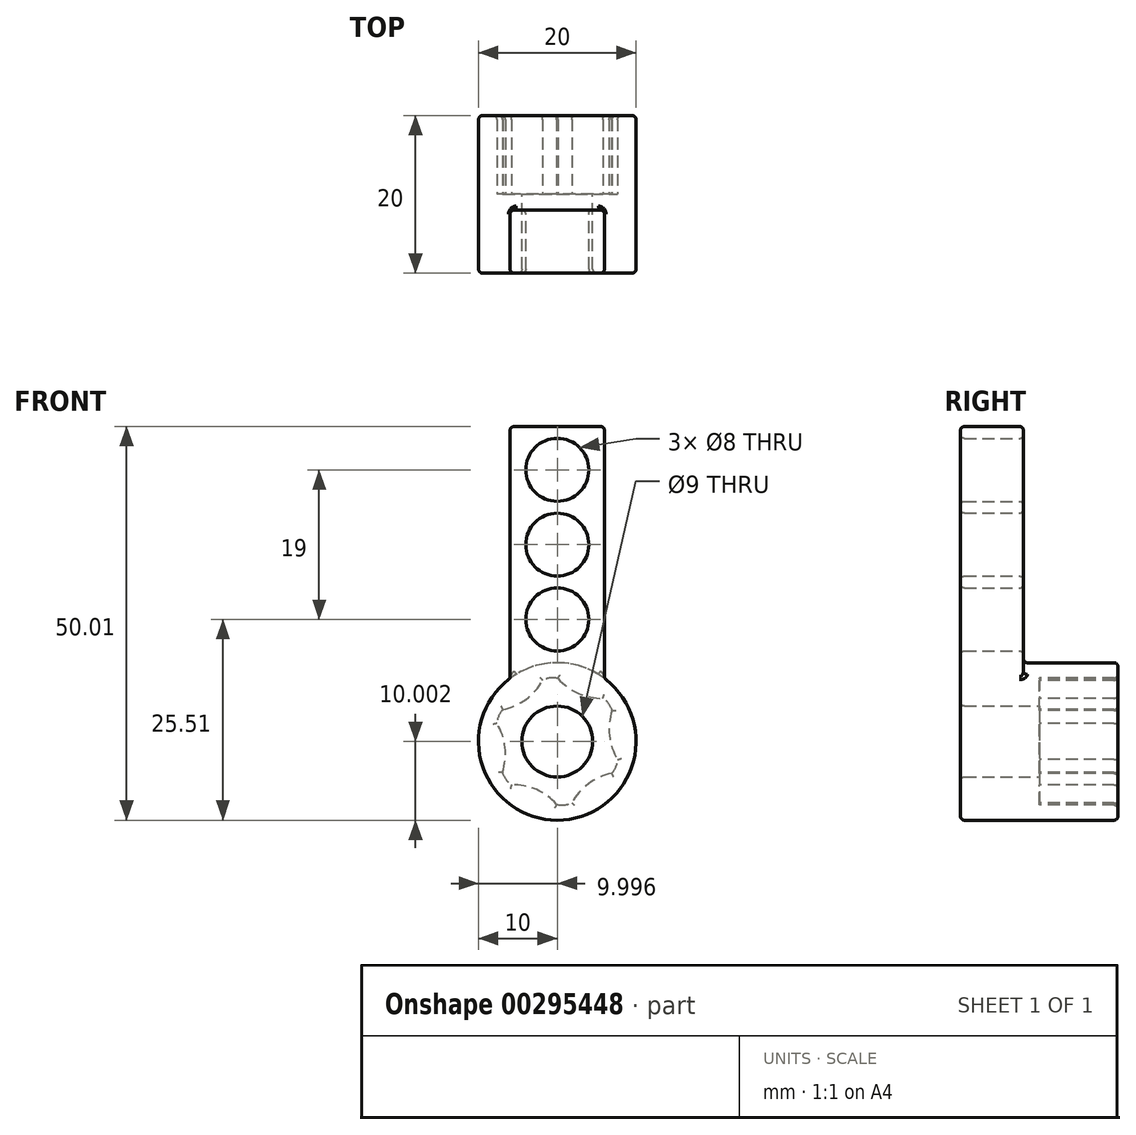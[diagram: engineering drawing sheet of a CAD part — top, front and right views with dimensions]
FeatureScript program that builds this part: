
annotation { "Feature Type Name" : "Feature", "Feature Type Description" : "" }
export const myFeature = defineFeature(function(context is Context, id is Id, definition is map)
    precondition{}
    {
        {
            var Q0;
            Q0=qCreatedBy(makeId("Front.planeOp"),FACE);
            var sketch = newSketch(context, id + "F0", { "sketchPlane" : qUnion([Q0])});
            skArc(sketch, "E0", {"start": v(0.06, 8) * mm, "mid": v(-0.91, 8.06) * mm, "end": v(-1.85, 7.78) * mm});
            skArc(sketch, "E1", {"start": v(6.96, 3.93) * mm, "mid": v(6.53, 4.81) * mm, "end": v(5.81, 5.48) * mm});
            skArc(sketch, "E2", {"start": v(0.06, 8) * mm, "mid": v(2.66, 6.1) * mm, "end": v(5.81, 5.48) * mm});
            skArc(sketch, "E3", {"start": v(-6.9, 4.05) * mm, "mid": v(-3.97, 5.36) * mm, "end": v(-1.85, 7.78) * mm});
            skArc(sketch, "E4", {"start": v(-6.97, -3.95) * mm, "mid": v(-6.63, -0.76) * mm, "end": v(-7.67, 2.28) * mm});
            skArc(sketch, "E5", {"start": v(-0.07, -8) * mm, "mid": v(-2.67, -6.12) * mm, "end": v(-5.82, -5.5) * mm});
            skArc(sketch, "E6", {"start": v(6.9, -4.07) * mm, "mid": v(3.96, -5.38) * mm, "end": v(1.84, -7.8) * mm});
            skArc(sketch, "E7", {"start": v(6.96, 3.93) * mm, "mid": v(6.63, 0.74) * mm, "end": v(7.66, -2.3) * mm});
            skCircle(sketch, "E8", {"center": v(0, 0) * mm, "radius": 10 * mm});
            skPoint(sketch, "E9.0.midPoint", {"position": v(2.1, 4.8) * mm});
            skCircle(sketch, "E10.cCircle", {"center": v(0, 0) * mm, "radius": 4.6 * mm, "construction": true});
            skLineSegment(sketch, "E10.0", {"start": v(0.6, -5.29) * mm, "end": v(-4.28, -3.16) * mm});
            skLineSegment(sketch, "E10.1", {"start": v(-4.28, -3.16) * mm, "end": v(-4.87, 2.12) * mm});
            skLineSegment(sketch, "E10.2", {"start": v(-4.87, 2.12) * mm, "end": v(-0.6, 5.27) * mm});
            skLineSegment(sketch, "E10.3", {"start": v(-0.6, 5.27) * mm, "end": v(4.27, 3.15) * mm});
            skLineSegment(sketch, "E10.4", {"start": v(4.27, 3.15) * mm, "end": v(4.87, -2.13) * mm});
            skLineSegment(sketch, "E10.5", {"start": v(4.87, -2.13) * mm, "end": v(0.6, -5.29) * mm});
            skPoint(sketch, "E10.0.midPoint", {"position": v(-1.84, -4.22) * mm});
            skArc(sketch, "E11.trimOffspring", {"start": v(6.9, -4.07) * mm, "mid": v(7.44, -3.25) * mm, "end": v(7.66, -2.3) * mm});
            skArc(sketch, "E12.trimOffspring", {"start": v(-0.07, -8) * mm, "mid": v(0.9, -8.07) * mm, "end": v(1.84, -7.8) * mm});
            skArc(sketch, "E13.trimOffspring", {"start": v(-6.97, -3.95) * mm, "mid": v(-6.53, -4.83) * mm, "end": v(-5.82, -5.5) * mm});
            skArc(sketch, "E14.trimOffspring", {"start": v(-6.9, 4.05) * mm, "mid": v(-7.44, 3.24) * mm, "end": v(-7.67, 2.28) * mm});
            skPoint(sketch, "E15.orphan", {"position": v(4.87, 3.6) * mm});
            skPoint(sketch, "E9.0.start.orphan", {"position": v(-0.68, 6.02) * mm});
            skSolve(sketch);
        }
        {
            var Q0;
            Q0=makeQuery(id+"F0.imprint","IMPRINT",FACE,{"disambiguationData":[TD([[makeQuery(id+"F0.imprint","IMPRINT",EDGE,{"derivedFrom":sQuery(id+"F0.wireOp",EDGE,"E0")}),-1.0]])]});
            var Q1;
            Q1=makeQuery(id+"F0.imprint","IMPRINT",FACE,{"disambiguationData":[TD([[makeQuery(id+"F0.imprint","IMPRINT",EDGE,{"derivedFrom":sQuery(id+"F0.wireOp",EDGE,"E10.0")}),-1.0]])]});
            var Q2;
            Q2=makeQuery(id+"F0.imprint","IMPRINT",FACE,{"disambiguationData":[TD([[makeQuery(id+"F0.imprint","IMPRINT",EDGE,{"derivedFrom":sQuery(id+"F0.wireOp",EDGE,"E0")}),1.0]])]});
            extrude(context, id + "F1", {"entities" : qUnion([Q0, Q1, Q2]), "offsetDistance" : 25 * mm, "depth" : 2 * mm});
        }
        {
            var Q0;
            Q0=makeQuery(id+"F0.imprint","IMPRINT",FACE,{"disambiguationData":[TD([[makeQuery(id+"F0.imprint","IMPRINT",EDGE,{"derivedFrom":sQuery(id+"F0.wireOp",EDGE,"E0")}),-1.0]])]});
            extrude(context, id + "F2", {"entities" : qUnion([Q0]), "operationType" : NewBodyOperationType.ADD, "oppositeDirection" : true, "offsetDistance" : 25 * mm, "depth" : 10 * mm});
        }
        {
            var Q0;
            Q0=makeQuery(id+"F1.opExtrude","CAP_FACE",FACE,{"disambiguationData":[OSD([sQuery(id+"F0.wireOp",EDGE,"E8")])],"isStart":false});
            var sketch = newSketch(context, id + "F3", { "sketchPlane" : qUnion([Q0])});
            skLineSegment(sketch, "E16", {"start": v(0, 0) * mm, "end": v(0, -10) * mm});
            skLineSegment(sketch, "E17", {"start": v(0, -10) * mm, "end": v(0, 10) * mm});
            skLineSegment(sketch, "E18.bottom", {"start": v(0, 0) * mm, "end": v(6, 0) * mm});
            skLineSegment(sketch, "E18.top", {"start": v(0, 40) * mm, "end": v(6, 40) * mm});
            skLineSegment(sketch, "E18.left", {"start": v(0, 0) * mm, "end": v(0, 40) * mm});
            skLineSegment(sketch, "E18.right", {"start": v(6, 0) * mm, "end": v(6, 40) * mm});
            skLineSegment(sketch, "E19.bottom", {"start": v(0, 0) * mm, "end": v(-6, 0) * mm});
            skLineSegment(sketch, "E19.top", {"start": v(0, 40) * mm, "end": v(-6, 40) * mm});
            skLineSegment(sketch, "E19.right", {"start": v(-6, 0) * mm, "end": v(-6, 40) * mm});
            skLineSegment(sketch, "E20.bottom", {"start": v(-6, 0) * mm, "end": v(6, 0) * mm});
            skCircle(sketch, "E21", {"center": v(0, 34.5) * mm, "radius": 4 * mm});
            skCircle(sketch, "E22", {"center": v(0, 25) * mm, "radius": 4 * mm});
            skCircle(sketch, "E23", {"center": v(0, 15.5) * mm, "radius": 4 * mm});
            skSolve(sketch);
        }
        {
            var Q0;
            {var subQ1=sQuery(id+"F3.wireOp",EDGE,"E20.top");Q0=makeQuery(id+"F3.imprint","IMPRINT",FACE,{"disambiguationData":[TD([[makeQuery(id+"F3.imprint","IMPRINT",EDGE,{"derivedFrom":subQ1}),1.0]])]});}
            var Q1;
            {var subQ0=sQuery(id+"F3.wireOp",EDGE,"E19.top");Q1=makeQuery(id+"F3.imprint","IMPRINT",FACE,{"disambiguationData":[TD([[makeQuery(id+"F3.imprint","IMPRINT",EDGE,{"derivedFrom":subQ0}),1.0]])]});}
            var Q2;
            {var subQ0=sQuery(id+"F3.wireOp",EDGE,"E18.top");Q2=makeQuery(id+"F3.imprint","IMPRINT",FACE,{"disambiguationData":[TD([[makeQuery(id+"F3.imprint","IMPRINT",EDGE,{"derivedFrom":subQ0}),-1.0]])]});}
            var Q3;
            {var subQ1=sQuery(id+"F3.wireOp",EDGE,"E18.right");var subQ3=makeQuery(id+"F1.opExtrude","CAP_EDGE",EDGE,{"disambiguationData":[OSD([sQuery(id+"F0.wireOp",EDGE,"E8")])],"isStart":false});var subQ4=makeQuery(id+"F3.imprint","INTERSECT",VERTEX,{"derivedFrom":[subQ3,subQ1]});Q3=makeQuery(id+"F3.imprint","IMPRINT",FACE,{"disambiguationData":[TD([[makeQuery(id+"F3.imprint","IMPRINT",EDGE,{"disambiguationData":[TD([[subQ4,1.0]])],"derivedFrom":subQ3}),1.0]])]});}
            var Q4;
            {var subQ1=sQuery(id+"F3.wireOp",EDGE,"E19.right");var subQ3=makeQuery(id+"F1.opExtrude","CAP_EDGE",EDGE,{"disambiguationData":[OSD([sQuery(id+"F0.wireOp",EDGE,"E8")])],"isStart":false});var subQ4=makeQuery(id+"F3.imprint","INTERSECT",VERTEX,{"derivedFrom":[subQ3,subQ1]});Q4=makeQuery(id+"F3.imprint","IMPRINT",FACE,{"disambiguationData":[TD([[makeQuery(id+"F3.imprint","IMPRINT",EDGE,{"disambiguationData":[TD([[subQ4,-1.0]])],"derivedFrom":subQ3}),1.0]])]});}
            var Q5;
            {var subQ1=sQuery(id+"F3.wireOp",EDGE,"E18.left");var subQ3=makeQuery(id+"F1.opExtrude","CAP_EDGE",EDGE,{"disambiguationData":[OSD([sQuery(id+"F0.wireOp",EDGE,"E8")])],"isStart":false});var subQ4=makeQuery(id+"F3.imprint","INTERSECT",VERTEX,{"derivedFrom":[subQ3,subQ1]});Q5=makeQuery(id+"F3.imprint","IMPRINT",FACE,{"disambiguationData":[TD([[makeQuery(id+"F3.imprint","IMPRINT",EDGE,{"disambiguationData":[TD([[subQ4,-1.0]])],"derivedFrom":subQ3}),1.0]])]});}
            var Q6;
            {var subQ3=makeQuery(id+"F1.opExtrude","CAP_EDGE",EDGE,{"disambiguationData":[OSD([sQuery(id+"F0.wireOp",EDGE,"E8")])],"isStart":false});var subQ5=sQuery(id+"F3.wireOp",EDGE,"E18.left");var subQ7=makeQuery(id+"F3.imprint","INTERSECT",VERTEX,{"derivedFrom":[subQ3,subQ5]});Q6=makeQuery(id+"F3.imprint","IMPRINT",FACE,{"disambiguationData":[TD([[makeQuery(id+"F3.imprint","IMPRINT",EDGE,{"disambiguationData":[TD([[subQ7,1.0]])],"derivedFrom":subQ3}),1.0]])]});}
            var Q7;
            {var subQ0=sQuery(id+"F3.wireOp",EDGE,"E17");var subQ1=makeQuery(id+"F1.opExtrude","CAP_EDGE",EDGE,{"disambiguationData":[OSD([sQuery(id+"F0.wireOp",EDGE,"E8")])],"isStart":false});var subQ2=makeQuery(id+"F3.imprint","INTERSECT",VERTEX,{"derivedFrom":[subQ1,subQ0]});Q7=makeQuery(id+"F3.imprint","IMPRINT",FACE,{"disambiguationData":[TD([[makeQuery(id+"F3.imprint","IMPRINT",EDGE,{"disambiguationData":[TD([[subQ2,1.0]])],"derivedFrom":subQ1}),1.0]])]});}
            var Q8;
            {var subQ0=sQuery(id+"F3.wireOp",EDGE,"E17");var subQ1=makeQuery(id+"F1.opExtrude","CAP_EDGE",EDGE,{"disambiguationData":[OSD([sQuery(id+"F0.wireOp",EDGE,"E8")])],"isStart":false});var subQ2=makeQuery(id+"F3.imprint","INTERSECT",VERTEX,{"derivedFrom":[subQ1,subQ0]});Q8=makeQuery(id+"F3.imprint","IMPRINT",FACE,{"disambiguationData":[TD([[makeQuery(id+"F3.imprint","IMPRINT",EDGE,{"disambiguationData":[TD([[subQ2,-1.0]])],"derivedFrom":subQ1}),1.0]])]});}
            extrude(context, id + "F4", {"entities" : qUnion([Q0, Q1, Q2, Q3, Q4, Q5, Q6, Q7, Q8]), "operationType" : NewBodyOperationType.ADD, "offsetDistance" : 25 * mm, "depth" : 8 * mm});
        }
        {
            var Q0;
            Q0=sQuery(id+"F0.wireOp",VERTEX,"E8.center");
            var Q1;
            Q1=makeQuery(id+"F1.opExtrude","SWEPT_BODY",BODY,{"disambiguationData":[OSD([sQuery(id+"F0.wireOp",EDGE,"E8")])]});
            hole(context, id + "F5", {"style" : HoleStyle.SIMPLE, "endStyle" : HoleEndStyle.THROUGH, "oppositeDirection" : true, "holeDiameter" : 9 * mm, "majorDiameter" : 5 * mm, "isTappedThrough" : true, "tappedDepth" : 12 * mm, "tapClearance" : 3, "locations" : qUnion([Q0]), "scope" : qUnion([Q1])});
        }
        {
            var Q0;
            Q0=makeQuery(id+"F4.opExtrude","SWEPT_FACE",FACE,{"disambiguationData":[OSD([sQuery(id+"F3.wireOp",EDGE,"E19.right")])]});
            var Q1;
            Q1=makeQuery(id+"F4.opExtrude","SWEPT_FACE",FACE,{"disambiguationData":[OSD([sQuery(id+"F3.wireOp",EDGE,"E18.top"),sQuery(id+"F3.wireOp",EDGE,"E19.top")])]});
            var Q2;
            Q2=makeQuery(id+"F4.opExtrude","SWEPT_FACE",FACE,{"disambiguationData":[OSD([sQuery(id+"F3.wireOp",EDGE,"E18.right")])]});
            var Q3;
            Q3=makeQuery(id+"F5.hole-0.boolean.opBoolean","COPY",FACE,{"derivedFrom":makeQuery(id+"F5.hole-0.opRevolve","SWEPT_FACE",FACE,{"disambiguationData":[OSD([sQuery(id+"F5.hole-0.sketch.wireOp",EDGE,"core_line_2")])]})});
            var Q4;
            Q4=makeQuery(id+"F4.opExtrude","CAP_FACE",FACE,{"disambiguationData":[OSD([sQuery(id+"F0.wireOp",EDGE,"E8"),sQuery(id+"F3.wireOp",EDGE,"E18.top"),sQuery(id+"F3.wireOp",EDGE,"E18.right"),sQuery(id+"F3.wireOp",EDGE,"E19.top"),sQuery(id+"F3.wireOp",EDGE,"E19.right"),sQuery(id+"F3.wireOp",EDGE,"E21"),sQuery(id+"F3.wireOp",EDGE,"E22"),sQuery(id+"F3.wireOp",EDGE,"E23")])],"isStart":true});
            var Q5;
            Q5=makeQuery(id+"F4.opExtrude","CAP_FACE",FACE,{"disambiguationData":[OSD([sQuery(id+"F0.wireOp",EDGE,"E8"),sQuery(id+"F3.wireOp",EDGE,"E18.top"),sQuery(id+"F3.wireOp",EDGE,"E18.right"),sQuery(id+"F3.wireOp",EDGE,"E19.top"),sQuery(id+"F3.wireOp",EDGE,"E19.right"),sQuery(id+"F3.wireOp",EDGE,"E21"),sQuery(id+"F3.wireOp",EDGE,"E22"),sQuery(id+"F3.wireOp",EDGE,"E23")])],"isStart":false});
            var Q6;
            Q6=makeQuery(id+"F2.opExtrude","CAP_FACE",FACE,{"disambiguationData":[OSD([sQuery(id+"F0.wireOp",EDGE,"E0"),sQuery(id+"F0.wireOp",EDGE,"E1"),sQuery(id+"F0.wireOp",EDGE,"E2"),sQuery(id+"F0.wireOp",EDGE,"E3"),sQuery(id+"F0.wireOp",EDGE,"E4"),sQuery(id+"F0.wireOp",EDGE,"E5"),sQuery(id+"F0.wireOp",EDGE,"E6"),sQuery(id+"F0.wireOp",EDGE,"E7"),sQuery(id+"F0.wireOp",EDGE,"E8"),sQuery(id+"F0.wireOp",EDGE,"E11.trimOffspring"),sQuery(id+"F0.wireOp",EDGE,"E12.trimOffspring"),sQuery(id+"F0.wireOp",EDGE,"E13.trimOffspring"),sQuery(id+"F0.wireOp",EDGE,"E14.trimOffspring")])],"isStart":false});
            fillet(context, id + "F6", {"entities" : qUnion([Q0, Q1, Q2, Q3, Q4, Q5, Q6]), "radius" : 0.5 * mm, "tangentPropagation" : true, "allowEdgeOverflow" : false});
        }
    });
